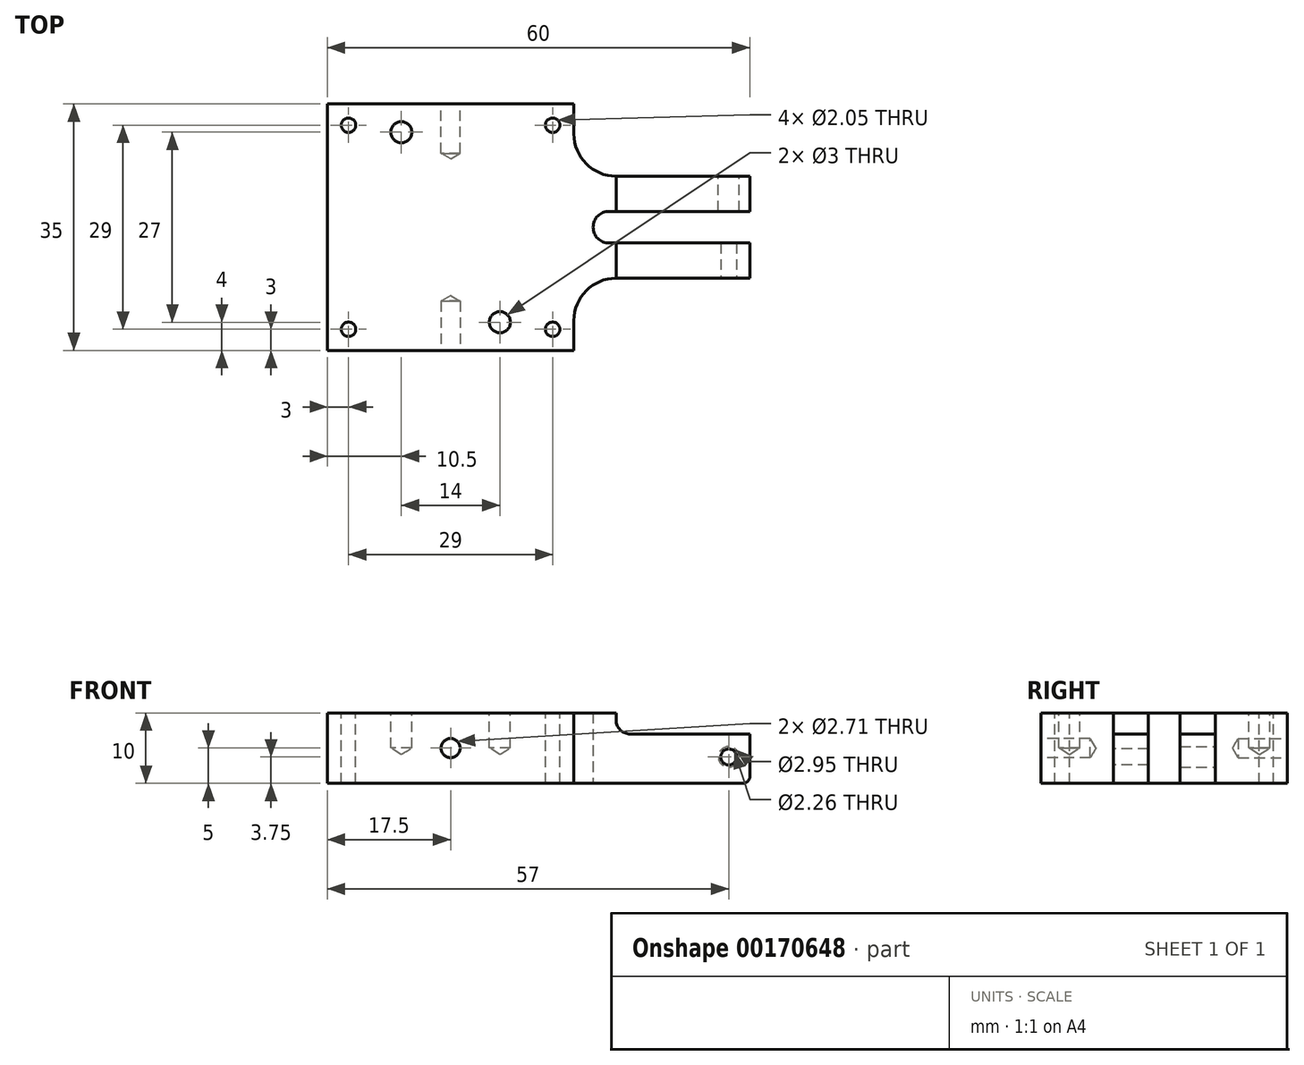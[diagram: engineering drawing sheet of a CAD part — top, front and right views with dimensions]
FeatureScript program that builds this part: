
annotation { "Feature Type Name" : "Feature", "Feature Type Description" : "" }
export const myFeature = defineFeature(function(context is Context, id is Id, definition is map)
    precondition{}
    {
        {
            var Q0;
            Q0=qCreatedBy(makeId("Top.planeOp"),FACE);
            var sketch = newSketch(context, id + "F0", { "sketchPlane" : qUnion([Q0])});
            skLineSegment(sketch, "E0.bottom", {"start": v(0, 0) * mm, "end": v(35, 0) * mm});
            skLineSegment(sketch, "E0.top", {"start": v(0, 35) * mm, "end": v(35, 35) * mm});
            skLineSegment(sketch, "E0.left", {"start": v(0, 0) * mm, "end": v(0, 35) * mm});
            skLineSegment(sketch, "E0.right", {"start": v(60, 10.25) * mm, "end": v(60, 15.25) * mm});
            skLineSegment(sketch, "E1.top", {"start": v(60, 10.25) * mm, "end": v(35, 10.25) * mm});
            skLineSegment(sketch, "E1.right", {"start": v(35, 0) * mm, "end": v(35, 10.25) * mm});
            skLineSegment(sketch, "E2.top", {"start": v(60, 24.75) * mm, "end": v(35, 24.75) * mm});
            skLineSegment(sketch, "E2.right", {"start": v(35, 35) * mm, "end": v(35, 24.75) * mm});
            skLineSegment(sketch, "E3.bottom", {"start": v(60, 15.25) * mm, "end": v(40, 15.25) * mm});
            skLineSegment(sketch, "E3.top", {"start": v(60, 19.75) * mm, "end": v(40, 19.75) * mm});
            skArc(sketch, "E4", {"start": v(40, 15.25) * mm, "mid": v(37.75, 17.5) * mm, "end": v(40, 19.75) * mm});
            skLineSegment(sketch, "E5.trimOffspring", {"start": v(60, 19.75) * mm, "end": v(60, 24.75) * mm});
            skSolve(sketch);
        }
        {
            var Q0;
            Q0 = qSketchRegion(id + "F0", true);
            extrude(context, id + "F1", {"entities" : qUnion([Q0]), "depth" : 10 * mm});
        }
        {
            var Q0;
            Q0=makeQuery(id+"F1.opExtrude","CAP_FACE",FACE,{"disambiguationData":[OSD([sQuery(id+"F0.wireOp",EDGE,"E0.bottom"),sQuery(id+"F0.wireOp",EDGE,"E0.top"),sQuery(id+"F0.wireOp",EDGE,"E0.left"),sQuery(id+"F0.wireOp",EDGE,"E0.right")])],"isStart":false});
            var sketch = newSketch(context, id + "F2", { "sketchPlane" : qUnion([Q0])});
            skPoint(sketch, "E6", {"position": v(3, 3) * mm});
            skPoint(sketch, "E7", {"position": v(32, 3) * mm});
            skPoint(sketch, "E8", {"position": v(32, 32) * mm});
            skPoint(sketch, "E9", {"position": v(3, 32) * mm});
            skPoint(sketch, "E10", {"position": v(10.5, 31) * mm});
            skPoint(sketch, "E11", {"position": v(24.5, 4) * mm});
            skSolve(sketch);
        }
        {
            var Q0;
            Q0=sQuery(id+"F2.wireOp",VERTEX,"E9");
            var Q1;
            Q1=sQuery(id+"F2.wireOp",VERTEX,"E8");
            var Q2;
            Q2=sQuery(id+"F2.wireOp",VERTEX,"E7");
            var Q3;
            Q3=sQuery(id+"F2.wireOp",VERTEX,"E6");
            var Q4;
            Q4=makeQuery(id+"F1.opExtrude","SWEPT_BODY",BODY,{"disambiguationData":[OSD([sQuery(id+"F0.wireOp",EDGE,"E0.bottom"),sQuery(id+"F0.wireOp",EDGE,"E0.top"),sQuery(id+"F0.wireOp",EDGE,"E0.left"),sQuery(id+"F0.wireOp",EDGE,"E0.right")])]});
            hole(context, id + "F3", {"style" : HoleStyle.SIMPLE, "endStyle" : HoleEndStyle.THROUGH, "holeDiameter" : 2.05 * mm, "locations" : qUnion([Q0, Q1, Q2, Q3]), "scope" : qUnion([Q4]), "isTappedThrough" : true});
        }
        {
            var Q0;
            Q0=sQuery(id+"F2.wireOp",VERTEX,"E10");
            var Q1;
            Q1=sQuery(id+"F2.wireOp",VERTEX,"E11");
            var Q2;
            Q2=makeQuery(id+"F1.opExtrude","SWEPT_BODY",BODY,{"disambiguationData":[OSD([sQuery(id+"F0.wireOp",EDGE,"E0.bottom"),sQuery(id+"F0.wireOp",EDGE,"E0.top"),sQuery(id+"F0.wireOp",EDGE,"E0.left"),sQuery(id+"F0.wireOp",EDGE,"E0.right")])]});
            hole(context, id + "F4", {"style" : HoleStyle.SIMPLE, "endStyle" : HoleEndStyle.BLIND, "holeDiameter" : 3 * mm, "holeDepth" : 5 * mm, "locations" : qUnion([Q0, Q1]), "scope" : qUnion([Q2])});
        }
        {
            var Q0;
            Q0=makeQuery(id+"F1.opExtrude","SWEPT_EDGE",EDGE,{"disambiguationData":[OSD([sQuery(id+"F0.wireOp",EDGE,"E1.top"),sQuery(id+"F0.wireOp",EDGE,"E1.right")])]});
            var Q1;
            Q1=makeQuery(id+"F1.opExtrude","SWEPT_EDGE",EDGE,{"disambiguationData":[OSD([sQuery(id+"F0.wireOp",EDGE,"E2.top"),sQuery(id+"F0.wireOp",EDGE,"E2.right")])]});
            fillet(context, id + "F5", {"entities" : qUnion([Q0, Q1]), "radius" : 6 * mm, "tangentPropagation" : true, "allowEdgeOverflow" : false});
        }
        {
            var Q0;
            Q0=makeQuery(id+"F1.opExtrude","SWEPT_FACE",FACE,{"disambiguationData":[OSD([sQuery(id+"F0.wireOp",EDGE,"E1.top")])]});
            var sketch = newSketch(context, id + "F6", { "sketchPlane" : qUnion([Q0])});
            skLineSegment(sketch, "E12", {"start": v(60, 7) * mm, "end": v(43, 7) * mm});
            skLineSegment(sketch, "E13", {"start": v(41, 9) * mm, "end": v(41, 10) * mm});
            skPoint(sketch, "E14.visualSharp", {"position": v(41, 7) * mm});
            skArc(sketch, "E14.filletArc", {"start": v(41, 9) * mm, "mid": v(41.59, 7.59) * mm, "end": v(43, 7) * mm});
            skLineSegment(sketch, "E15", {"start": v(41, 10) * mm, "end": v(60, 10) * mm});
            skLineSegment(sketch, "E16", {"start": v(60, 10) * mm, "end": v(60, 7) * mm});
            skSolve(sketch);
        }
        {
            var Q0;
            Q0 = qSketchRegion(id + "F6", true);
            extrude(context, id + "F7", {"entities" : qUnion([Q0]), "operationType" : NewBodyOperationType.REMOVE, "endBound" : BoundingType.THROUGH_ALL, "oppositeDirection" : true, "depth" : 25 * mm});
        }
        {
            var Q0;
            {var subQ0=sQuery(id+"F0.wireOp",EDGE,"E0.right");var subQ1=sQuery(id+"F6.wireOp",EDGE,"E12");var subQ2=sQuery(id+"F0.wireOp",EDGE,"E1.top");Q0=makeQuery(id+"F7.boolean.opBoolean","COPY",EDGE,{"disambiguationData":[TD([makeQuery(id+"F1.opExtrude","SWEPT_FACE",FACE,{"disambiguationData":[OSD([subQ0])]})])],"derivedFrom":makeQuery(id+"F7.opExtrude","SWEPT_EDGE",EDGE,{"disambiguationData":[OSD([subQ0,subQ2,subQ1,sQuery(id+"F6.wireOp",EDGE,"E16")])]})});}
            var Q1;
            {var subQ0=sQuery(id+"F6.wireOp",EDGE,"E12");Q1=makeQuery(id+"F7.boolean.opBoolean","COPY",EDGE,{"disambiguationData":[TD([makeQuery(id+"F1.opExtrude","SWEPT_FACE",FACE,{"disambiguationData":[OSD([sQuery(id+"F0.wireOp",EDGE,"E2.top")])]})])],"derivedFrom":makeQuery(id+"F7.opExtrude","SWEPT_EDGE",EDGE,{"disambiguationData":[OSD([sQuery(id+"F0.wireOp",EDGE,"E0.right"),sQuery(id+"F0.wireOp",EDGE,"E1.top"),subQ0,sQuery(id+"F6.wireOp",EDGE,"E16")])]})});}
            var Q2;
            Q2=makeQuery(id+"F1.opExtrude","CAP_EDGE",EDGE,{"disambiguationData":[OSD([sQuery(id+"F0.wireOp",EDGE,"E5.trimOffspring")])],"isStart":true});
            var Q3;
            Q3=makeQuery(id+"F1.opExtrude","CAP_EDGE",EDGE,{"disambiguationData":[OSD([sQuery(id+"F0.wireOp",EDGE,"E0.right")])],"isStart":true});
            fillet(context, id + "F8", {"entities" : qUnion([Q0, Q1, Q2, Q3]), "radius" : 1 * mm, "tangentPropagation" : true, "allowEdgeOverflow" : false});
        }
        {
            var Q0;
            Q0=makeQuery(id+"F1.opExtrude","SWEPT_FACE",FACE,{"disambiguationData":[OSD([sQuery(id+"F0.wireOp",EDGE,"E2.top")])]});
            var sketch = newSketch(context, id + "F9", { "sketchPlane" : qUnion([Q0])});
            skPoint(sketch, "E17", {"position": v(-57, 3.75) * mm});
            skSolve(sketch);
        }
        {
            var Q0;
            Q0=sQuery(id+"F9.wireOp",VERTEX,"E17");
            var Q1;
            Q1=makeQuery(id+"F1.opExtrude","SWEPT_BODY",BODY,{"disambiguationData":[OSD([sQuery(id+"F0.wireOp",EDGE,"E0.bottom"),sQuery(id+"F0.wireOp",EDGE,"E0.top"),sQuery(id+"F0.wireOp",EDGE,"E0.left"),sQuery(id+"F0.wireOp",EDGE,"E0.right"),sQuery(id+"F0.wireOp",EDGE,"E1.top"),sQuery(id+"F0.wireOp",EDGE,"E1.right"),sQuery(id+"F0.wireOp",EDGE,"E2.top"),sQuery(id+"F0.wireOp",EDGE,"E2.right"),sQuery(id+"F0.wireOp",EDGE,"E3.bottom"),sQuery(id+"F0.wireOp",EDGE,"E3.top"),sQuery(id+"F0.wireOp",EDGE,"E4"),sQuery(id+"F0.wireOp",EDGE,"E5.trimOffspring")])]});
            hole(context, id + "F10", {"style" : HoleStyle.SIMPLE, "endStyle" : HoleEndStyle.BLIND, "holeDiameter" : 2.95 * mm, "holeDepth" : 5 * mm, "locations" : qUnion([Q0]), "scope" : qUnion([Q1])});
        }
        {
            var Q0;
            Q0=makeQuery(id+"F1.opExtrude","SWEPT_FACE",FACE,{"disambiguationData":[OSD([sQuery(id+"F0.wireOp",EDGE,"E1.top")])]});
            var sketch = newSketch(context, id + "F11", { "sketchPlane" : qUnion([Q0])});
            skPoint(sketch, "E18", {"position": v(57, 3.75) * mm});
            skSolve(sketch);
        }
        {
            var Q0;
            Q0=sQuery(id+"F11.wireOp",VERTEX,"E18");
            var Q1;
            Q1=makeQuery(id+"F1.opExtrude","SWEPT_BODY",BODY,{"disambiguationData":[OSD([sQuery(id+"F0.wireOp",EDGE,"E0.bottom"),sQuery(id+"F0.wireOp",EDGE,"E0.top"),sQuery(id+"F0.wireOp",EDGE,"E0.left"),sQuery(id+"F0.wireOp",EDGE,"E0.right"),sQuery(id+"F0.wireOp",EDGE,"E1.top"),sQuery(id+"F0.wireOp",EDGE,"E1.right"),sQuery(id+"F0.wireOp",EDGE,"E2.top"),sQuery(id+"F0.wireOp",EDGE,"E2.right"),sQuery(id+"F0.wireOp",EDGE,"E3.bottom"),sQuery(id+"F0.wireOp",EDGE,"E3.top"),sQuery(id+"F0.wireOp",EDGE,"E4"),sQuery(id+"F0.wireOp",EDGE,"E5.trimOffspring")])]});
            hole(context, id + "F12", {"style" : HoleStyle.SIMPLE, "endStyle" : HoleEndStyle.BLIND, "standardTappedOrClearance" : lookupTablePath({ "standard" : "ANSI", "engagement" : "75%", "pitch" : "40 tpi", "size" : "#4", "type" : "Tapped" }), "standardBlindInLast" : lookupTablePath({ "standard" : "ANSI", "engagement" : "75%", "pitch" : "40 tpi", "size" : "#4", "type" : "Tapped" }), "holeDiameter" : 2.26 * mm, "holeDepth" : 5 * mm, "locations" : qUnion([Q0]), "scope" : qUnion([Q1]), "majorDiameter" : 2.84 * mm});
        }
        {
            var Q0;
            Q0=makeQuery(id+"F1.opExtrude","SWEPT_FACE",FACE,{"disambiguationData":[OSD([sQuery(id+"F0.wireOp",EDGE,"E0.top")])]});
            var sketch = newSketch(context, id + "F13", { "sketchPlane" : qUnion([Q0])});
            skPoint(sketch, "E19", {"position": v(-17.5, 5) * mm});
            skPoint(sketch, "E19.positionSnap0", {"position": v(-35, 5) * mm});
            skPoint(sketch, "E19.positionSnap1", {"position": v(-17.5, 10) * mm});
            skSolve(sketch);
        }
        {
            var Q0;
            Q0=makeQuery(id+"F1.opExtrude","SWEPT_FACE",FACE,{"disambiguationData":[OSD([sQuery(id+"F0.wireOp",EDGE,"E0.bottom")])]});
            var sketch = newSketch(context, id + "F14", { "sketchPlane" : qUnion([Q0])});
            skPoint(sketch, "E20", {"position": v(17.5, 5) * mm});
            skPoint(sketch, "E20.positionSnap0", {"position": v(35, 5) * mm});
            skPoint(sketch, "E20.positionSnap1", {"position": v(17.5, 10) * mm});
            skSolve(sketch);
        }
        {
            var Q0;
            Q0=sQuery(id+"F13.wireOp",VERTEX,"E19");
            var Q1;
            Q1=sQuery(id+"F14.wireOp",VERTEX,"E20");
            var Q2;
            Q2=makeQuery(id+"F1.opExtrude","SWEPT_BODY",BODY,{"disambiguationData":[OSD([sQuery(id+"F0.wireOp",EDGE,"E0.bottom"),sQuery(id+"F0.wireOp",EDGE,"E0.top"),sQuery(id+"F0.wireOp",EDGE,"E0.left"),sQuery(id+"F0.wireOp",EDGE,"E0.right"),sQuery(id+"F0.wireOp",EDGE,"E1.top"),sQuery(id+"F0.wireOp",EDGE,"E1.right"),sQuery(id+"F0.wireOp",EDGE,"E2.top"),sQuery(id+"F0.wireOp",EDGE,"E2.right"),sQuery(id+"F0.wireOp",EDGE,"E3.bottom"),sQuery(id+"F0.wireOp",EDGE,"E3.top"),sQuery(id+"F0.wireOp",EDGE,"E4"),sQuery(id+"F0.wireOp",EDGE,"E5.trimOffspring")])]});
            hole(context, id + "F15", {"style" : HoleStyle.SIMPLE, "endStyle" : HoleEndStyle.BLIND, "standardTappedOrClearance" : lookupTablePath({ "standard" : "ANSI", "engagement" : "75%", "pitch" : "32 tpi", "size" : "#6", "type" : "Tapped" }), "standardBlindInLast" : lookupTablePath({ "standard" : "ANSI", "engagement" : "75%", "pitch" : "32 tpi", "size" : "#6", "type" : "Tapped" }), "holeDiameter" : 2.7 * mm, "holeDepth" : 7 * mm, "locations" : qUnion([Q0, Q1]), "scope" : qUnion([Q2]), "majorDiameter" : 3.5 * mm});
        }
    });
